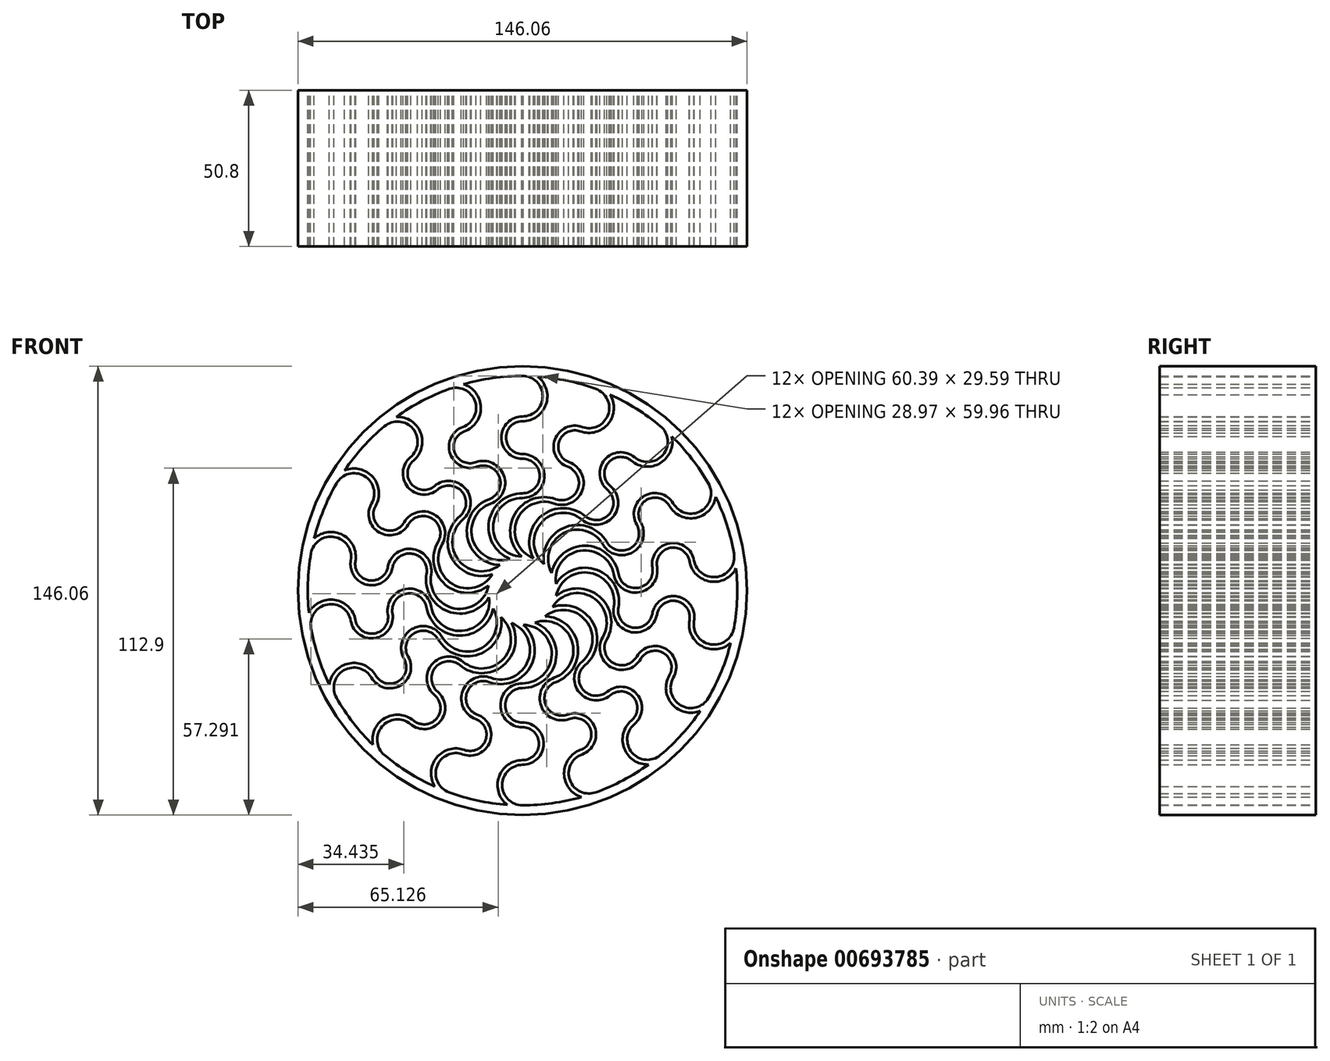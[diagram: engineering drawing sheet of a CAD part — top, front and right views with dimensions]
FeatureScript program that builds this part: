
annotation { "Feature Type Name" : "Feature", "Feature Type Description" : "" }
export const myFeature = defineFeature(function(context is Context, id is Id, definition is map)
    precondition{}
    {
        {
            var Q0;
            Q0=qCreatedBy(makeId("Front.planeOp"),FACE);
            var sketch = newSketch(context, id + "F0", { "sketchPlane" : qUnion([Q0])});
            skArc(sketch, "E0", {"start": v(0, 69.85) * mm, "mid": v(-9.67, 69.18) * mm, "end": v(-19.16, 67.17) * mm});
            skArc(sketch, "E1", {"start": v(0, 44.45) * mm, "mid": v(7.14, 37.3) * mm, "end": v(0, 30.16) * mm});
            skArc(sketch, "E2", {"start": v(0, 30.16) * mm, "mid": v(-9.52, 20.77) * mm, "end": v(-0.26, 11.12) * mm});
            skArc(sketch, "E3", {"start": v(0, 44.45) * mm, "mid": v(-5.36, 49.8) * mm, "end": v(0, 55.17) * mm});
            skArc(sketch, "E4", {"start": v(4.97, 69.67) * mm, "mid": v(7.67, 60.64) * mm, "end": v(0, 55.17) * mm});
            skArc(sketch, "E5.0", {"start": v(0, 31.69) * mm, "mid": v(-10.86, 22.7) * mm, "end": v(-4.05, 10.36) * mm});
            skArc(sketch, "E5.1", {"start": v(0, 42.93) * mm, "mid": v(5.62, 37.3) * mm, "end": v(0, 31.69) * mm});
            skArc(sketch, "E5.2", {"start": v(0, 42.93) * mm, "mid": v(-6.88, 49.8) * mm, "end": v(0, 56.69) * mm});
            skArc(sketch, "E5.3", {"start": v(0, 69.85) * mm, "mid": v(6.58, 63.27) * mm, "end": v(0, 56.69) * mm});
            skCircle(sketch, "E6", {"center": v(0, 0) * mm, "radius": 73.03 * mm});
            skPoint(sketch, "E7.orphan", {"position": v(0, 71.37) * mm});
            skPoint(sketch, "E8.1.0", {"position": v(-24.41, 67.07) * mm});
            skArc(sketch, "E8.1.1", {"start": v(-15.2, 41.77) * mm, "mid": v(-6.05, 37.5) * mm, "end": v(-10.32, 28.34) * mm});
            skArc(sketch, "E8.1.2", {"start": v(-10.32, 28.34) * mm, "mid": v(-16.05, 16.26) * mm, "end": v(-4.05, 10.36) * mm});
            skArc(sketch, "E8.1.3", {"start": v(-15.2, 41.77) * mm, "mid": v(-22.07, 44.97) * mm, "end": v(-18.87, 51.84) * mm});
            skArc(sketch, "E8.1.4", {"start": v(-19.16, 67.17) * mm, "mid": v(-13.54, 59.6) * mm, "end": v(-18.87, 51.84) * mm});
            skArc(sketch, "E8.1.5", {"start": v(-10.84, 29.78) * mm, "mid": v(-17.96, 17.62) * mm, "end": v(-7.35, 8.35) * mm});
            skArc(sketch, "E8.1.6", {"start": v(-14.68, 40.34) * mm, "mid": v(-7.48, 36.98) * mm, "end": v(-10.84, 29.78) * mm});
            skArc(sketch, "E8.1.7", {"start": v(-14.68, 40.34) * mm, "mid": v(-23.5, 44.45) * mm, "end": v(-19.39, 53.27) * mm});
            skArc(sketch, "E8.1.8", {"start": v(-23.9, 65.64) * mm, "mid": v(-15.46, 61.7) * mm, "end": v(-19.39, 53.27) * mm});
            skPoint(sketch, "E8.2.0", {"position": v(-45.88, 54.68) * mm});
            skArc(sketch, "E8.2.1", {"start": v(-28.57, 34.05) * mm, "mid": v(-18.5, 33.17) * mm, "end": v(-19.39, 23.1) * mm});
            skArc(sketch, "E8.2.2", {"start": v(-19.39, 23.1) * mm, "mid": v(-20.65, 9.79) * mm, "end": v(-7.35, 8.35) * mm});
            skArc(sketch, "E8.2.3", {"start": v(-28.57, 34.05) * mm, "mid": v(-36.12, 34.71) * mm, "end": v(-35.46, 42.26) * mm});
            skArc(sketch, "E8.2.4", {"start": v(-40.98, 56.57) * mm, "mid": v(-33.1, 51.38) * mm, "end": v(-35.46, 42.26) * mm});
            skArc(sketch, "E8.2.5", {"start": v(-20.37, 24.27) * mm, "mid": v(-22.9, 10.4) * mm, "end": v(-9.76, 5.33) * mm});
            skArc(sketch, "E8.2.6", {"start": v(-27.6, 32.88) * mm, "mid": v(-19.68, 32.2) * mm, "end": v(-20.37, 24.27) * mm});
            skArc(sketch, "E8.2.7", {"start": v(-27.6, 32.88) * mm, "mid": v(-37.29, 33.73) * mm, "end": v(-36.44, 43.43) * mm});
            skArc(sketch, "E8.2.8", {"start": v(-44.9, 53.5) * mm, "mid": v(-35.63, 52.7) * mm, "end": v(-36.44, 43.43) * mm});
            skArc(sketch, "E9.1.3.0", {"start": v(-38.5, 22.23) * mm, "mid": v(-28.74, 24.84) * mm, "end": v(-26.12, 15.08) * mm});
            skArc(sketch, "E9.5.3.0", {"start": v(-26.12, 15.08) * mm, "mid": v(-22.75, 2.14) * mm, "end": v(-9.76, 5.33) * mm});
            skArc(sketch, "E9.9.3.0", {"start": v(-38.5, 22.23) * mm, "mid": v(-45.81, 20.26) * mm, "end": v(-47.77, 27.58) * mm});
            skArc(sketch, "E9.13.3.0", {"start": v(-57.86, 39.14) * mm, "mid": v(-48.69, 36.96) * mm, "end": v(-47.77, 27.58) * mm});
            skArc(sketch, "E9.17.3.0", {"start": v(-27.44, 15.84) * mm, "mid": v(-25.08, 1.95) * mm, "end": v(-11, 1.67) * mm});
            skPoint(sketch, "E9.20.3.0", {"position": v(-61.81, 35.69) * mm});
            skArc(sketch, "E9.21.3.0", {"start": v(-37.18, 21.46) * mm, "mid": v(-29.5, 23.52) * mm, "end": v(-27.44, 15.84) * mm});
            skArc(sketch, "E9.25.3.0", {"start": v(-37.18, 21.46) * mm, "mid": v(-46.58, 18.94) * mm, "end": v(-49.1, 28.34) * mm});
            skArc(sketch, "E9.29.3.0", {"start": v(-60.5, 34.93) * mm, "mid": v(-51.5, 37.33) * mm, "end": v(-49.1, 28.34) * mm});
            skArc(sketch, "E9.1.4.0", {"start": v(-43.77, 7.72) * mm, "mid": v(-35.5, 13.51) * mm, "end": v(-29.7, 5.24) * mm});
            skArc(sketch, "E9.5.4.0", {"start": v(-29.7, 5.24) * mm, "mid": v(-22.1, -5.77) * mm, "end": v(-11, 1.67) * mm});
            skArc(sketch, "E9.9.4.0", {"start": v(-43.77, 7.72) * mm, "mid": v(-49.98, 3.37) * mm, "end": v(-54.33, 9.58) * mm});
            skArc(sketch, "E9.13.4.0", {"start": v(-67.75, 17) * mm, "mid": v(-58.4, 18.08) * mm, "end": v(-54.33, 9.58) * mm});
            skArc(sketch, "E9.17.4.0", {"start": v(-31.2, 5.5) * mm, "mid": v(-24.24, -6.75) * mm, "end": v(-10.9, -2.19) * mm});
            skPoint(sketch, "E9.20.4.0", {"position": v(-70.29, 12.4) * mm});
            skArc(sketch, "E9.21.4.0", {"start": v(-42.27, 7.45) * mm, "mid": v(-35.76, 12.01) * mm, "end": v(-31.2, 5.5) * mm});
            skArc(sketch, "E9.25.4.0", {"start": v(-42.27, 7.45) * mm, "mid": v(-50.25, 1.87) * mm, "end": v(-55.83, 9.84) * mm});
            skArc(sketch, "E9.29.4.0", {"start": v(-68.79, 12.13) * mm, "mid": v(-61.17, 17.47) * mm, "end": v(-55.83, 9.84) * mm});
            skArc(sketch, "E9.1.5.0", {"start": v(-43.77, -7.72) * mm, "mid": v(-37.98, 0.56) * mm, "end": v(-29.7, -5.24) * mm});
            skArc(sketch, "E9.5.5.0", {"start": v(-29.7, -5.24) * mm, "mid": v(-18.8, -12.99) * mm, "end": v(-10.9, -2.19) * mm});
            skArc(sketch, "E9.9.5.0", {"start": v(-43.77, -7.72) * mm, "mid": v(-48.12, -13.93) * mm, "end": v(-54.33, -9.58) * mm});
            skArc(sketch, "E9.13.5.0", {"start": v(-69.48, -7.2) * mm, "mid": v(-61.05, -2.98) * mm, "end": v(-54.33, -9.58) * mm});
            skArc(sketch, "E9.17.5.0", {"start": v(-31.2, -5.5) * mm, "mid": v(-20.47, -14.63) * mm, "end": v(-9.5, -5.78) * mm});
            skPoint(sketch, "E9.20.5.0", {"position": v(-70.29, -12.4) * mm});
            skArc(sketch, "E9.21.5.0", {"start": v(-42.27, -7.45) * mm, "mid": v(-37.72, -0.94) * mm, "end": v(-31.2, -5.5) * mm});
            skArc(sketch, "E9.25.5.0", {"start": v(-42.27, -7.45) * mm, "mid": v(-47.86, -15.43) * mm, "end": v(-55.83, -9.84) * mm});
            skArc(sketch, "E9.29.5.0", {"start": v(-68.79, -12.13) * mm, "mid": v(-63.45, -4.5) * mm, "end": v(-55.83, -9.84) * mm});
            skArc(sketch, "E9.1.6.0", {"start": v(-38.5, -22.22) * mm, "mid": v(-35.88, -12.47) * mm, "end": v(-26.12, -15.08) * mm});
            skArc(sketch, "E9.5.6.0", {"start": v(-26.12, -15.08) * mm, "mid": v(-13.22, -18.63) * mm, "end": v(-9.5, -5.78) * mm});
            skArc(sketch, "E9.9.6.0", {"start": v(-38.5, -22.22) * mm, "mid": v(-40.46, -29.54) * mm, "end": v(-47.77, -27.58) * mm});
            skArc(sketch, "E9.13.6.0", {"start": v(-62.82, -30.53) * mm, "mid": v(-56.35, -23.68) * mm, "end": v(-47.77, -27.58) * mm});
            skArc(sketch, "E9.17.6.0", {"start": v(-27.44, -15.84) * mm, "mid": v(-14.23, -20.75) * mm, "end": v(-6.95, -8.68) * mm});
            skPoint(sketch, "E9.20.6.0", {"position": v(-61.81, -35.69) * mm});
            skArc(sketch, "E9.21.6.0", {"start": v(-37.18, -21.46) * mm, "mid": v(-35.12, -13.79) * mm, "end": v(-27.44, -15.84) * mm});
            skArc(sketch, "E9.25.6.0", {"start": v(-37.18, -21.46) * mm, "mid": v(-39.7, -30.86) * mm, "end": v(-49.1, -28.34) * mm});
            skArc(sketch, "E9.29.6.0", {"start": v(-60.5, -34.92) * mm, "mid": v(-58.08, -25.94) * mm, "end": v(-49.1, -28.34) * mm});
            skArc(sketch, "E9.1.7.0", {"start": v(-28.57, -34.05) * mm, "mid": v(-29.45, -23.99) * mm, "end": v(-19.39, -23.1) * mm});
            skArc(sketch, "E9.5.7.0", {"start": v(-19.39, -23.1) * mm, "mid": v(-6.05, -22.03) * mm, "end": v(-6.95, -8.68) * mm});
            skArc(sketch, "E9.9.7.0", {"start": v(-28.57, -34.05) * mm, "mid": v(-27.91, -41.6) * mm, "end": v(-35.46, -42.26) * mm});
            skArc(sketch, "E9.13.7.0", {"start": v(-48.6, -50.18) * mm, "mid": v(-44.85, -41.53) * mm, "end": v(-35.46, -42.26) * mm});
            skArc(sketch, "E9.17.7.0", {"start": v(-20.37, -24.27) * mm, "mid": v(-6.27, -24.36) * mm, "end": v(-3.56, -10.53) * mm});
            skPoint(sketch, "E9.20.7.0", {"position": v(-45.88, -54.68) * mm});
            skArc(sketch, "E9.21.7.0", {"start": v(-27.6, -32.88) * mm, "mid": v(-28.28, -24.97) * mm, "end": v(-20.37, -24.27) * mm});
            skArc(sketch, "E9.25.7.0", {"start": v(-27.6, -32.88) * mm, "mid": v(-26.74, -42.58) * mm, "end": v(-36.44, -43.43) * mm});
            skArc(sketch, "E9.29.7.0", {"start": v(-44.9, -53.5) * mm, "mid": v(-45.7, -44.24) * mm, "end": v(-36.44, -43.43) * mm});
            skArc(sketch, "E9.1.8.0", {"start": v(-15.2, -41.77) * mm, "mid": v(-19.47, -32.61) * mm, "end": v(-10.32, -28.34) * mm});
            skArc(sketch, "E9.5.8.0", {"start": v(-10.32, -28.34) * mm, "mid": v(1.85, -22.77) * mm, "end": v(-3.56, -10.53) * mm});
            skArc(sketch, "E9.9.8.0", {"start": v(-15.2, -41.77) * mm, "mid": v(-12, -48.64) * mm, "end": v(-18.87, -51.84) * mm});
            skArc(sketch, "E9.13.8.0", {"start": v(-28.5, -63.77) * mm, "mid": v(-27.95, -54.36) * mm, "end": v(-18.87, -51.84) * mm});
            skArc(sketch, "E9.17.8.0", {"start": v(-10.84, -29.78) * mm, "mid": v(2.44, -25.04) * mm, "end": v(0.26, -11.12) * mm});
            skPoint(sketch, "E9.20.8.0", {"position": v(-24.41, -67.07) * mm});
            skArc(sketch, "E9.21.8.0", {"start": v(-14.68, -40.34) * mm, "mid": v(-18.04, -33.13) * mm, "end": v(-10.84, -29.78) * mm});
            skArc(sketch, "E9.25.8.0", {"start": v(-14.68, -40.34) * mm, "mid": v(-10.57, -49.16) * mm, "end": v(-19.39, -53.27) * mm});
            skArc(sketch, "E9.29.8.0", {"start": v(-23.9, -65.64) * mm, "mid": v(-27.82, -57.2) * mm, "end": v(-19.39, -53.27) * mm});
            skArc(sketch, "E9.1.9.0", {"start": v(0, -44.45) * mm, "mid": v(-7.14, -37.3) * mm, "end": v(0, -30.16) * mm});
            skArc(sketch, "E9.5.9.0", {"start": v(0, -30.16) * mm, "mid": v(9.52, -20.77) * mm, "end": v(0.26, -11.12) * mm});
            skArc(sketch, "E9.9.9.0", {"start": v(0, -44.45) * mm, "mid": v(5.36, -49.8) * mm, "end": v(0, -55.17) * mm});
            skArc(sketch, "E9.13.9.0", {"start": v(-4.97, -69.67) * mm, "mid": v(-7.67, -60.64) * mm, "end": v(0, -55.17) * mm});
            skArc(sketch, "E9.17.9.0", {"start": v(0, -31.69) * mm, "mid": v(10.86, -22.7) * mm, "end": v(4.05, -10.36) * mm});
            skPoint(sketch, "E9.20.9.0", {"position": v(0, -71.37) * mm});
            skArc(sketch, "E9.21.9.0", {"start": v(0, -42.93) * mm, "mid": v(-5.62, -37.3) * mm, "end": v(0, -31.69) * mm});
            skArc(sketch, "E9.25.9.0", {"start": v(0, -42.93) * mm, "mid": v(6.88, -49.8) * mm, "end": v(0, -56.69) * mm});
            skArc(sketch, "E9.29.9.0", {"start": v(0, -69.85) * mm, "mid": v(-6.58, -63.27) * mm, "end": v(0, -56.69) * mm});
            skArc(sketch, "E9.1.10.0", {"start": v(15.2, -41.77) * mm, "mid": v(6.05, -37.5) * mm, "end": v(10.32, -28.34) * mm});
            skArc(sketch, "E9.5.10.0", {"start": v(10.32, -28.34) * mm, "mid": v(16.05, -16.26) * mm, "end": v(4.05, -10.36) * mm});
            skArc(sketch, "E9.9.10.0", {"start": v(15.2, -41.77) * mm, "mid": v(22.07, -44.97) * mm, "end": v(18.87, -51.84) * mm});
            skArc(sketch, "E9.13.10.0", {"start": v(19.16, -67.17) * mm, "mid": v(13.54, -59.6) * mm, "end": v(18.87, -51.84) * mm});
            skArc(sketch, "E9.17.10.0", {"start": v(10.84, -29.78) * mm, "mid": v(17.96, -17.62) * mm, "end": v(7.35, -8.35) * mm});
            skPoint(sketch, "E9.20.10.0", {"position": v(24.41, -67.07) * mm});
            skArc(sketch, "E9.21.10.0", {"start": v(14.68, -40.34) * mm, "mid": v(7.48, -36.98) * mm, "end": v(10.84, -29.78) * mm});
            skArc(sketch, "E9.25.10.0", {"start": v(14.68, -40.34) * mm, "mid": v(23.5, -44.45) * mm, "end": v(19.39, -53.27) * mm});
            skArc(sketch, "E9.29.10.0", {"start": v(23.9, -65.64) * mm, "mid": v(15.46, -61.7) * mm, "end": v(19.39, -53.27) * mm});
            skArc(sketch, "E9.1.11.0", {"start": v(28.57, -34.05) * mm, "mid": v(18.5, -33.17) * mm, "end": v(19.39, -23.1) * mm});
            skArc(sketch, "E9.5.11.0", {"start": v(19.39, -23.1) * mm, "mid": v(20.65, -9.79) * mm, "end": v(7.35, -8.35) * mm});
            skArc(sketch, "E9.9.11.0", {"start": v(28.57, -34.05) * mm, "mid": v(36.12, -34.71) * mm, "end": v(35.46, -42.26) * mm});
            skArc(sketch, "E9.13.11.0", {"start": v(40.98, -56.57) * mm, "mid": v(33.1, -51.38) * mm, "end": v(35.46, -42.26) * mm});
            skArc(sketch, "E9.17.11.0", {"start": v(20.37, -24.27) * mm, "mid": v(22.9, -10.4) * mm, "end": v(9.76, -5.33) * mm});
            skPoint(sketch, "E9.20.11.0", {"position": v(45.88, -54.68) * mm});
            skArc(sketch, "E9.21.11.0", {"start": v(27.6, -32.88) * mm, "mid": v(19.68, -32.2) * mm, "end": v(20.37, -24.27) * mm});
            skArc(sketch, "E9.25.11.0", {"start": v(27.6, -32.88) * mm, "mid": v(37.29, -33.73) * mm, "end": v(36.44, -43.43) * mm});
            skArc(sketch, "E9.29.11.0", {"start": v(44.9, -53.5) * mm, "mid": v(35.63, -52.7) * mm, "end": v(36.44, -43.43) * mm});
            skArc(sketch, "E10.1.12.0", {"start": v(38.5, -22.23) * mm, "mid": v(28.74, -24.84) * mm, "end": v(26.12, -15.08) * mm});
            skArc(sketch, "E10.5.12.0", {"start": v(26.12, -15.08) * mm, "mid": v(22.75, -2.14) * mm, "end": v(9.76, -5.33) * mm});
            skArc(sketch, "E10.9.12.0", {"start": v(38.5, -22.23) * mm, "mid": v(45.81, -20.26) * mm, "end": v(47.77, -27.58) * mm});
            skArc(sketch, "E10.13.12.0", {"start": v(57.86, -39.14) * mm, "mid": v(48.69, -36.96) * mm, "end": v(47.77, -27.58) * mm});
            skArc(sketch, "E10.17.12.0", {"start": v(27.44, -15.84) * mm, "mid": v(25.08, -1.95) * mm, "end": v(11, -1.67) * mm});
            skPoint(sketch, "E10.20.12.0", {"position": v(61.81, -35.69) * mm});
            skArc(sketch, "E10.21.12.0", {"start": v(37.18, -21.46) * mm, "mid": v(29.5, -23.52) * mm, "end": v(27.44, -15.84) * mm});
            skArc(sketch, "E10.25.12.0", {"start": v(37.18, -21.46) * mm, "mid": v(46.58, -18.94) * mm, "end": v(49.1, -28.34) * mm});
            skArc(sketch, "E10.29.12.0", {"start": v(60.5, -34.93) * mm, "mid": v(51.5, -37.33) * mm, "end": v(49.1, -28.34) * mm});
            skArc(sketch, "E10.1.13.0", {"start": v(43.77, -7.72) * mm, "mid": v(35.5, -13.51) * mm, "end": v(29.7, -5.24) * mm});
            skArc(sketch, "E10.5.13.0", {"start": v(29.7, -5.24) * mm, "mid": v(22.1, 5.77) * mm, "end": v(11, -1.67) * mm});
            skArc(sketch, "E10.9.13.0", {"start": v(43.77, -7.72) * mm, "mid": v(49.98, -3.37) * mm, "end": v(54.33, -9.58) * mm});
            skArc(sketch, "E10.13.13.0", {"start": v(67.75, -17) * mm, "mid": v(58.4, -18.08) * mm, "end": v(54.33, -9.58) * mm});
            skArc(sketch, "E10.17.13.0", {"start": v(31.2, -5.5) * mm, "mid": v(24.24, 6.75) * mm, "end": v(10.9, 2.19) * mm});
            skPoint(sketch, "E10.20.13.0", {"position": v(70.29, -12.4) * mm});
            skArc(sketch, "E10.21.13.0", {"start": v(42.27, -7.45) * mm, "mid": v(35.76, -12.01) * mm, "end": v(31.2, -5.5) * mm});
            skArc(sketch, "E10.25.13.0", {"start": v(42.27, -7.45) * mm, "mid": v(50.25, -1.87) * mm, "end": v(55.83, -9.84) * mm});
            skArc(sketch, "E10.29.13.0", {"start": v(68.79, -12.13) * mm, "mid": v(61.17, -17.47) * mm, "end": v(55.83, -9.84) * mm});
            skArc(sketch, "E10.1.14.0", {"start": v(43.77, 7.72) * mm, "mid": v(37.98, -0.56) * mm, "end": v(29.7, 5.24) * mm});
            skArc(sketch, "E10.5.14.0", {"start": v(29.7, 5.24) * mm, "mid": v(18.8, 12.99) * mm, "end": v(10.9, 2.19) * mm});
            skArc(sketch, "E10.9.14.0", {"start": v(43.77, 7.72) * mm, "mid": v(48.12, 13.93) * mm, "end": v(54.33, 9.58) * mm});
            skArc(sketch, "E10.13.14.0", {"start": v(69.48, 7.2) * mm, "mid": v(61.05, 2.98) * mm, "end": v(54.33, 9.58) * mm});
            skArc(sketch, "E10.17.14.0", {"start": v(31.2, 5.5) * mm, "mid": v(20.47, 14.63) * mm, "end": v(9.5, 5.78) * mm});
            skPoint(sketch, "E10.20.14.0", {"position": v(70.29, 12.4) * mm});
            skArc(sketch, "E10.21.14.0", {"start": v(42.27, 7.45) * mm, "mid": v(37.72, 0.94) * mm, "end": v(31.2, 5.5) * mm});
            skArc(sketch, "E10.25.14.0", {"start": v(42.27, 7.45) * mm, "mid": v(47.86, 15.43) * mm, "end": v(55.83, 9.84) * mm});
            skArc(sketch, "E10.29.14.0", {"start": v(68.79, 12.13) * mm, "mid": v(63.45, 4.5) * mm, "end": v(55.83, 9.84) * mm});
            skArc(sketch, "E10.1.15.0", {"start": v(38.5, 22.22) * mm, "mid": v(35.88, 12.47) * mm, "end": v(26.12, 15.08) * mm});
            skArc(sketch, "E10.5.15.0", {"start": v(26.12, 15.08) * mm, "mid": v(13.22, 18.63) * mm, "end": v(9.5, 5.78) * mm});
            skArc(sketch, "E10.9.15.0", {"start": v(38.5, 22.22) * mm, "mid": v(40.46, 29.54) * mm, "end": v(47.77, 27.58) * mm});
            skArc(sketch, "E10.13.15.0", {"start": v(62.82, 30.53) * mm, "mid": v(56.35, 23.68) * mm, "end": v(47.77, 27.58) * mm});
            skArc(sketch, "E10.17.15.0", {"start": v(27.44, 15.84) * mm, "mid": v(14.23, 20.75) * mm, "end": v(6.95, 8.68) * mm});
            skPoint(sketch, "E10.20.15.0", {"position": v(61.81, 35.69) * mm});
            skArc(sketch, "E10.21.15.0", {"start": v(37.18, 21.46) * mm, "mid": v(35.12, 13.79) * mm, "end": v(27.44, 15.84) * mm});
            skArc(sketch, "E10.25.15.0", {"start": v(37.18, 21.46) * mm, "mid": v(39.7, 30.86) * mm, "end": v(49.1, 28.34) * mm});
            skArc(sketch, "E10.29.15.0", {"start": v(60.5, 34.92) * mm, "mid": v(58.08, 25.94) * mm, "end": v(49.1, 28.34) * mm});
            skArc(sketch, "E11.1.16.0", {"start": v(28.57, 34.05) * mm, "mid": v(29.45, 23.99) * mm, "end": v(19.39, 23.1) * mm});
            skArc(sketch, "E11.5.16.0", {"start": v(19.39, 23.1) * mm, "mid": v(6.05, 22.03) * mm, "end": v(6.95, 8.68) * mm});
            skArc(sketch, "E11.9.16.0", {"start": v(28.57, 34.05) * mm, "mid": v(27.91, 41.6) * mm, "end": v(35.46, 42.26) * mm});
            skArc(sketch, "E11.13.16.0", {"start": v(48.6, 50.18) * mm, "mid": v(44.85, 41.53) * mm, "end": v(35.46, 42.26) * mm});
            skArc(sketch, "E11.17.16.0", {"start": v(20.37, 24.27) * mm, "mid": v(6.27, 24.36) * mm, "end": v(3.56, 10.53) * mm});
            skPoint(sketch, "E11.20.16.0", {"position": v(45.88, 54.68) * mm});
            skArc(sketch, "E11.21.16.0", {"start": v(27.6, 32.88) * mm, "mid": v(28.28, 24.97) * mm, "end": v(20.37, 24.27) * mm});
            skArc(sketch, "E11.25.16.0", {"start": v(27.6, 32.88) * mm, "mid": v(26.74, 42.58) * mm, "end": v(36.44, 43.43) * mm});
            skArc(sketch, "E11.29.16.0", {"start": v(44.9, 53.5) * mm, "mid": v(45.7, 44.24) * mm, "end": v(36.44, 43.43) * mm});
            skArc(sketch, "E11.1.17.0", {"start": v(15.2, 41.77) * mm, "mid": v(19.47, 32.61) * mm, "end": v(10.32, 28.34) * mm});
            skArc(sketch, "E11.5.17.0", {"start": v(10.32, 28.34) * mm, "mid": v(-1.85, 22.77) * mm, "end": v(3.56, 10.53) * mm});
            skArc(sketch, "E11.9.17.0", {"start": v(15.2, 41.77) * mm, "mid": v(12, 48.64) * mm, "end": v(18.87, 51.84) * mm});
            skArc(sketch, "E11.13.17.0", {"start": v(28.5, 63.77) * mm, "mid": v(27.95, 54.36) * mm, "end": v(18.87, 51.84) * mm});
            skArc(sketch, "E11.17.17.0", {"start": v(10.84, 29.78) * mm, "mid": v(-2.44, 25.04) * mm, "end": v(-0.26, 11.12) * mm});
            skPoint(sketch, "E11.20.17.0", {"position": v(24.41, 67.07) * mm});
            skArc(sketch, "E11.21.17.0", {"start": v(14.68, 40.34) * mm, "mid": v(18.04, 33.13) * mm, "end": v(10.84, 29.78) * mm});
            skArc(sketch, "E11.25.17.0", {"start": v(14.68, 40.34) * mm, "mid": v(10.57, 49.16) * mm, "end": v(19.39, 53.27) * mm});
            skArc(sketch, "E11.29.17.0", {"start": v(23.9, 65.64) * mm, "mid": v(27.82, 57.2) * mm, "end": v(19.39, 53.27) * mm});
            skArc(sketch, "E12.trimOffspring", {"start": v(-23.9, 65.64) * mm, "mid": v(-32.75, 61.7) * mm, "end": v(-40.98, 56.57) * mm});
            skArc(sketch, "E13.trimOffspring", {"start": v(-44.9, 53.5) * mm, "mid": v(-51.88, 46.77) * mm, "end": v(-57.86, 39.14) * mm});
            skArc(sketch, "E14.trimOffspring", {"start": v(-60.5, 34.92) * mm, "mid": v(-64.75, 26.21) * mm, "end": v(-67.75, 17) * mm});
            skArc(sketch, "E15.trimOffspring", {"start": v(-68.79, 12.13) * mm, "mid": v(-69.8, 2.49) * mm, "end": v(-69.48, -7.2) * mm});
            skArc(sketch, "E16.trimOffspring", {"start": v(-60.5, -34.92) * mm, "mid": v(-55.07, -42.97) * mm, "end": v(-48.6, -50.18) * mm});
            skArc(sketch, "E17.trimOffspring", {"start": v(-68.79, -12.13) * mm, "mid": v(-66.45, -21.54) * mm, "end": v(-62.82, -30.53) * mm});
            skArc(sketch, "E18.trimOffspring", {"start": v(-44.9, -53.5) * mm, "mid": v(-37.06, -59.21) * mm, "end": v(-28.5, -63.77) * mm});
            skArc(sketch, "E19.trimOffspring", {"start": v(-23.9, -65.64) * mm, "mid": v(-14.57, -68.31) * mm, "end": v(-4.97, -69.67) * mm});
            skArc(sketch, "E20.trimOffspring", {"start": v(0, -69.85) * mm, "mid": v(9.67, -69.18) * mm, "end": v(19.16, -67.17) * mm});
            skArc(sketch, "E21.trimOffspring", {"start": v(23.9, -65.64) * mm, "mid": v(32.75, -61.7) * mm, "end": v(40.98, -56.57) * mm});
            skArc(sketch, "E22.trimOffspring", {"start": v(44.9, -53.5) * mm, "mid": v(51.88, -46.77) * mm, "end": v(57.86, -39.14) * mm});
            skArc(sketch, "E23.trimOffspring", {"start": v(60.5, -34.93) * mm, "mid": v(64.75, -26.21) * mm, "end": v(67.75, -17) * mm});
            skArc(sketch, "E24.trimOffspring", {"start": v(68.79, -12.13) * mm, "mid": v(69.8, -2.49) * mm, "end": v(69.48, 7.2) * mm});
            skArc(sketch, "E25.trimOffspring", {"start": v(68.79, 12.13) * mm, "mid": v(66.45, 21.54) * mm, "end": v(62.82, 30.53) * mm});
            skArc(sketch, "E26.trimOffspring", {"start": v(60.5, 34.92) * mm, "mid": v(55.07, 42.97) * mm, "end": v(48.6, 50.18) * mm});
            skArc(sketch, "E27.trimOffspring", {"start": v(44.9, 53.5) * mm, "mid": v(37.06, 59.21) * mm, "end": v(28.5, 63.77) * mm});
            skArc(sketch, "E28.trimOffspring", {"start": v(23.9, 65.64) * mm, "mid": v(14.57, 68.31) * mm, "end": v(4.97, 69.67) * mm});
            skPoint(sketch, "E29.orphan", {"position": v(-3.8, -10.44) * mm});
            skPoint(sketch, "E30.orphan", {"position": v(0, -11.11) * mm});
            skPoint(sketch, "E31.orphan", {"position": v(3.8, -10.44) * mm});
            skPoint(sketch, "E32.orphan", {"position": v(7.14, -8.51) * mm});
            skPoint(sketch, "E33.orphan", {"position": v(9.62, -5.56) * mm});
            skPoint(sketch, "E34.orphan", {"position": v(10.94, -1.93) * mm});
            skPoint(sketch, "E35.orphan", {"position": v(10.94, 1.93) * mm});
            skPoint(sketch, "E36.orphan", {"position": v(9.62, 5.56) * mm});
            skPoint(sketch, "E37.orphan", {"position": v(7.14, 8.51) * mm});
            skPoint(sketch, "E38.orphan", {"position": v(3.8, 10.44) * mm});
            skPoint(sketch, "E39.orphan", {"position": v(-0.25, 11.1) * mm});
            skPoint(sketch, "E40.orphan", {"position": v(0, 11.11) * mm});
            skPoint(sketch, "E41.orphan", {"position": v(-4.04, 10.35) * mm});
            skPoint(sketch, "E42.orphan", {"position": v(-3.8, 10.44) * mm});
            skPoint(sketch, "E43.orphan", {"position": v(-10.94, 1.93) * mm});
            skPoint(sketch, "E44.orphan", {"position": v(-7.14, -8.51) * mm});
            skPoint(sketch, "E45.orphan", {"position": v(-9.62, -5.56) * mm});
            skPoint(sketch, "E46.orphan", {"position": v(-10.94, -1.93) * mm});
            skSolve(sketch);
        }
        {
            var Q0;
            Q0 = qSketchRegion(id + "F0", true);
            extrude(context, id + "F1", {"entities" : qUnion([Q0]), "depth" : 50.8 * mm, "offsetDistance" : 25.4 * mm});
        }
    });
